# Revit family: SLAB  PENDANT  LIGHT
name_source: partatom
category: Lighting Fixtures
units: mm (PartAtom-declared; Revit-internal decimal feet)

## family parameters
Cut with Voids When Loaded = No
Host = Face
Light Source = Yes
Part Type = Normal
Room Calculation Point = No
Round Connector Dimension = Use Diameter
Shared = No

## types (7) — shared parameters
Acoustic = White
Acoustic Body = Yes
Aircraft Cable Pendant Mount = Yes
Average life based on 77F(HRS) = 50000
CRI = >80
Color Filter = 16777215
Default Elevation = 0' - 0"
Description = The Slab Pendant Light, with its exceptionally thin profile appears to float across the ceiling landscape.
Dimming Lamp Color Temperature Shift = <None>
Finish/Color = WHITE PMMA
Fixture Height = 4' - 11"
Fixture Width = 0' - 5 7/8"
Hanger Gap = 0' - 4"
IP Rating = 20
Load Classification = Lighting
Manufacturer = Above All Lighting
Power Factor = 1
Tilt Angle = -90.00°
Type Comments = SLAB  PENDANT  LIGHT
URL = https://www.abovealllighting.com

## per-type parameters (varying)
| type | A | Apparent Load | Fixture Length | No. of Hanger | Order number | Photometric Web File | Wattage Comments |
| SLAB04-308-PM | 3' - 9 1/4" | 50 VA | 3' - 11 1/4" | 2 | 15992 | generic | 40 W |
| SLAB04-358-PM | 3' - 9 1/4" | 50 VA | 3' - 11 1/4" | 2 | 15993 | SLAB04-358-PM-277V_IESNA2002.IES | 40 W |
| SLAB04-408-PM | 3' - 9 1/4" | 50 VA | 3' - 11 1/4" | 2 | 15994 | generic | 40 W |
| SLAB04-SW8-PM | 3' - 9 1/4" | 50 VA | 3' - 11 1/4" | 2 | 15995 | generic | 40 W |
| SLAB08-308-PM | 7' - 8 15/32" | 100 VA | 7' - 10 15/32" | 3 | 15996 | generic | 80 W |
| SLAB08-358-PM | 7' - 8 15/32" | 100 VA | 7' - 10 15/32" | 3 | 15997 | generic | 80 W |
| SLAB08-408-PM | 7' - 8 15/32" | 100 VA | 7' - 10 15/32" | 3 | 15998 | generic | 80 W |

note: column(s) folded — value = type name in every type: Model

## geometry (parser evidence)
native form markers: Sweep x18
no freeform markers — native parametric forms only
